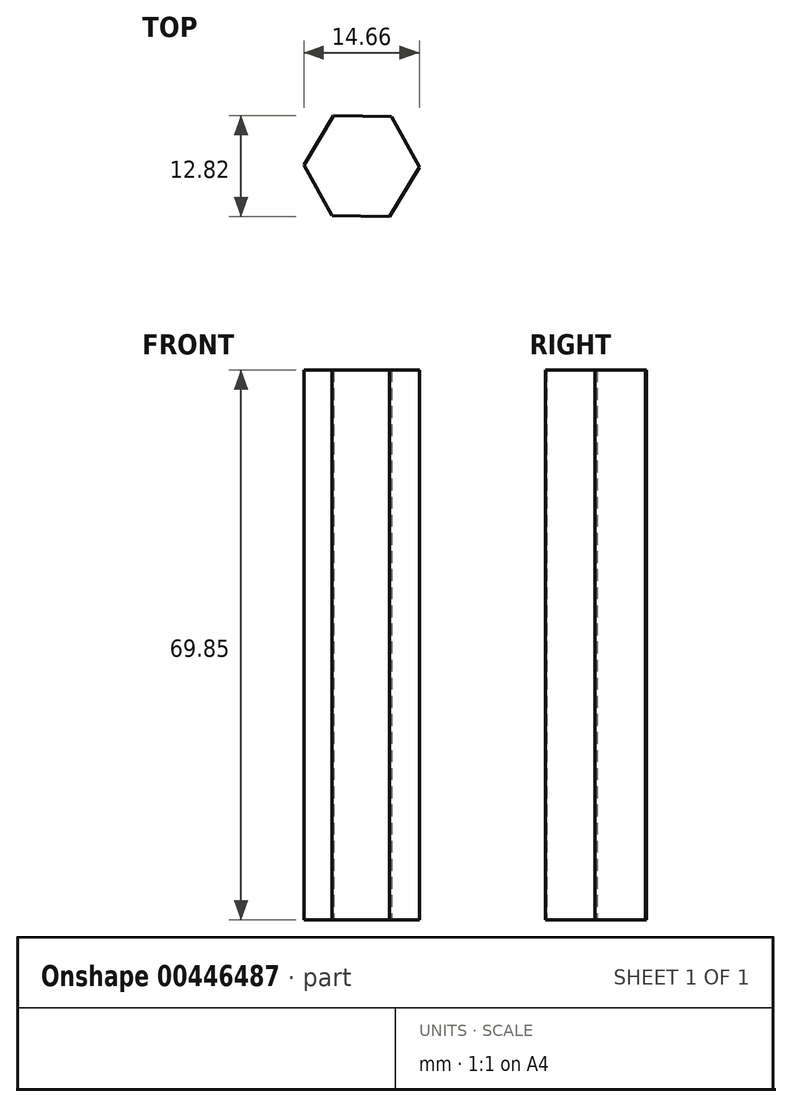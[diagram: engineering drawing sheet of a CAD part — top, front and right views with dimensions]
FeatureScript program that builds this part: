
annotation { "Feature Type Name" : "Feature", "Feature Type Description" : "" }
export const myFeature = defineFeature(function(context is Context, id is Id, definition is map)
    precondition{}
    {
        {
            var Q0;
            Q0=qCreatedBy(makeId("Top.planeOp"),FACE);
            var sketch = newSketch(context, id + "F0", { "sketchPlane" : qUnion([Q0])});
            skCircle(sketch, "E0.cCircle", {"center": v(0, 0) * mm, "radius": 6.35 * mm, "construction": true});
            skLineSegment(sketch, "E0.0", {"start": v(-7.33, 0.12) * mm, "end": v(-3.56, 6.41) * mm});
            skLineSegment(sketch, "E0.1", {"start": v(-3.56, 6.41) * mm, "end": v(3.77, 6.29) * mm});
            skLineSegment(sketch, "E0.2", {"start": v(3.77, 6.29) * mm, "end": v(7.33, -0.12) * mm});
            skLineSegment(sketch, "E0.3", {"start": v(7.33, -0.12) * mm, "end": v(3.56, -6.41) * mm});
            skLineSegment(sketch, "E0.4", {"start": v(3.56, -6.41) * mm, "end": v(-3.77, -6.29) * mm});
            skLineSegment(sketch, "E0.5", {"start": v(-3.77, -6.29) * mm, "end": v(-7.33, 0.12) * mm});
            skPoint(sketch, "E0.0.midPoint", {"position": v(-5.45, 3.27) * mm});
            skSolve(sketch);
        }
        {
            var Q0;
            Q0=makeQuery(id+"F0.imprint","IMPRINT",FACE,{"disambiguationData":[TD([[makeQuery(id+"F0.imprint","IMPRINT",EDGE,{"derivedFrom":sQuery(id+"F0.wireOp",EDGE,"E0.0")}),-1.0]])]});
            extrude(context, id + "F1", {"entities" : qUnion([Q0]), "depth" : 69.85 * mm});
        }
    });
